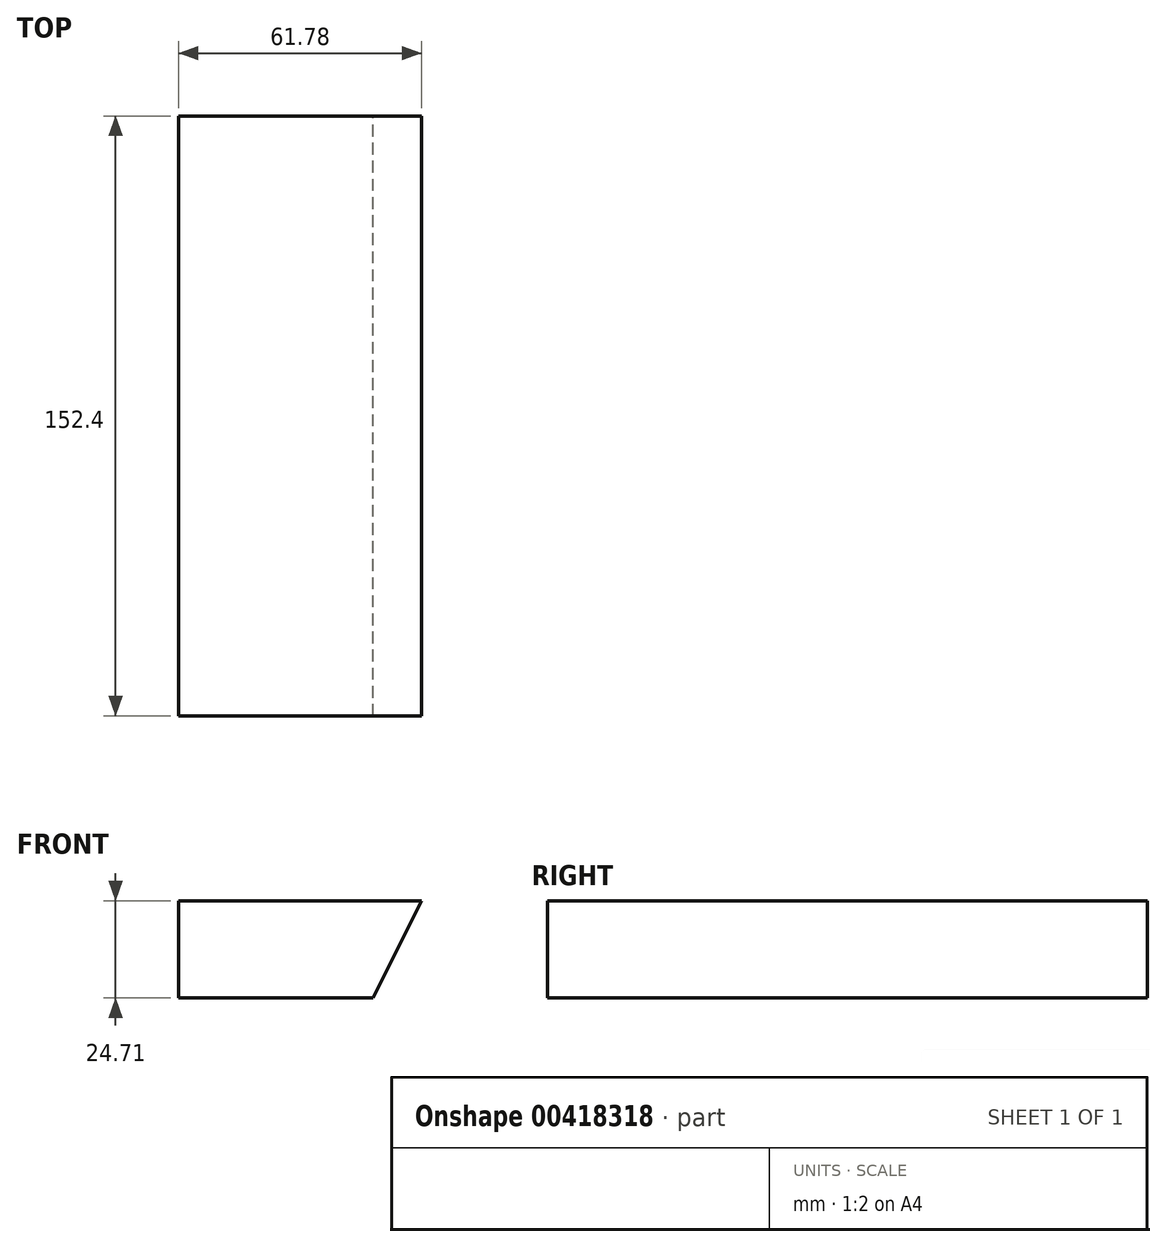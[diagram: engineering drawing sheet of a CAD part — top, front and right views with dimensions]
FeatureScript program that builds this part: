
annotation { "Feature Type Name" : "Feature", "Feature Type Description" : "" }
export const myFeature = defineFeature(function(context is Context, id is Id, definition is map)
    precondition{}
    {
        {
            var Q0;
            Q0=qCreatedBy(makeId("Front.planeOp"),FACE);
            var sketch = newSketch(context, id + "F0", { "sketchPlane" : qUnion([Q0])});
            skLineSegment(sketch, "E0.bottom", {"start": v(32.62, -16.9) * mm, "end": v(-32.62, -16.9) * mm});
            skLineSegment(sketch, "E0.top", {"start": v(32.62, 16.9) * mm, "end": v(-32.62, 16.9) * mm});
            skLineSegment(sketch, "E0.left", {"start": v(32.62, -16.9) * mm, "end": v(32.62, 16.9) * mm});
            skLineSegment(sketch, "E0.right", {"start": v(-32.62, -16.9) * mm, "end": v(-32.62, 16.9) * mm});
            skPoint(sketch, "E0.middle", {"position": v(0, 0) * mm});
            skLineSegment(sketch, "E1.bottom", {"start": v(63.5, 53.93) * mm, "end": v(1.73, 53.93) * mm});
            skLineSegment(sketch, "E1.top", {"start": v(63.5, 78.64) * mm, "end": v(1.73, 78.64) * mm});
            skLineSegment(sketch, "E1.left", {"start": v(63.5, 53.93) * mm, "end": v(63.5, 78.64) * mm});
            skLineSegment(sketch, "E1.right", {"start": v(1.73, 53.93) * mm, "end": v(1.73, 78.64) * mm});
            skPoint(sketch, "E1.middle", {"position": v(32.62, 66.28) * mm});
            skPoint(sketch, "E1.middle.positionSnap0", {"position": v(32.62, 0) * mm});
            skPoint(sketch, "E1.centerSnap0", {"position": v(32.62, 0) * mm});
            skLineSegment(sketch, "E2", {"start": v(32.62, 16.9) * mm, "end": v(63.5, 78.64) * mm});
            skLineSegment(sketch, "E3", {"start": v(63.5, 53.93) * mm, "end": v(32.62, -16.9) * mm});
            skLineSegment(sketch, "E4", {"start": v(1.73, 53.93) * mm, "end": v(-32.62, -16.9) * mm});
            skLineSegment(sketch, "E5", {"start": v(1.73, 78.64) * mm, "end": v(-32.62, 16.9) * mm});
            skSolve(sketch);
        }
        {
            var Q0;
            {var subQ4=sQuery(id+"F0.wireOp",EDGE,"E1.top");Q0=makeQuery(id+"F0.imprint","IMPRINT",FACE,{"disambiguationData":[TD([[makeQuery(id+"F0.imprint","IMPRINT",EDGE,{"derivedFrom":subQ4}),1.0]])]});}
            extrude(context, id + "F1", {"entities" : qUnion([Q0]), "depth" : 152.4 * mm});
        }
    });
